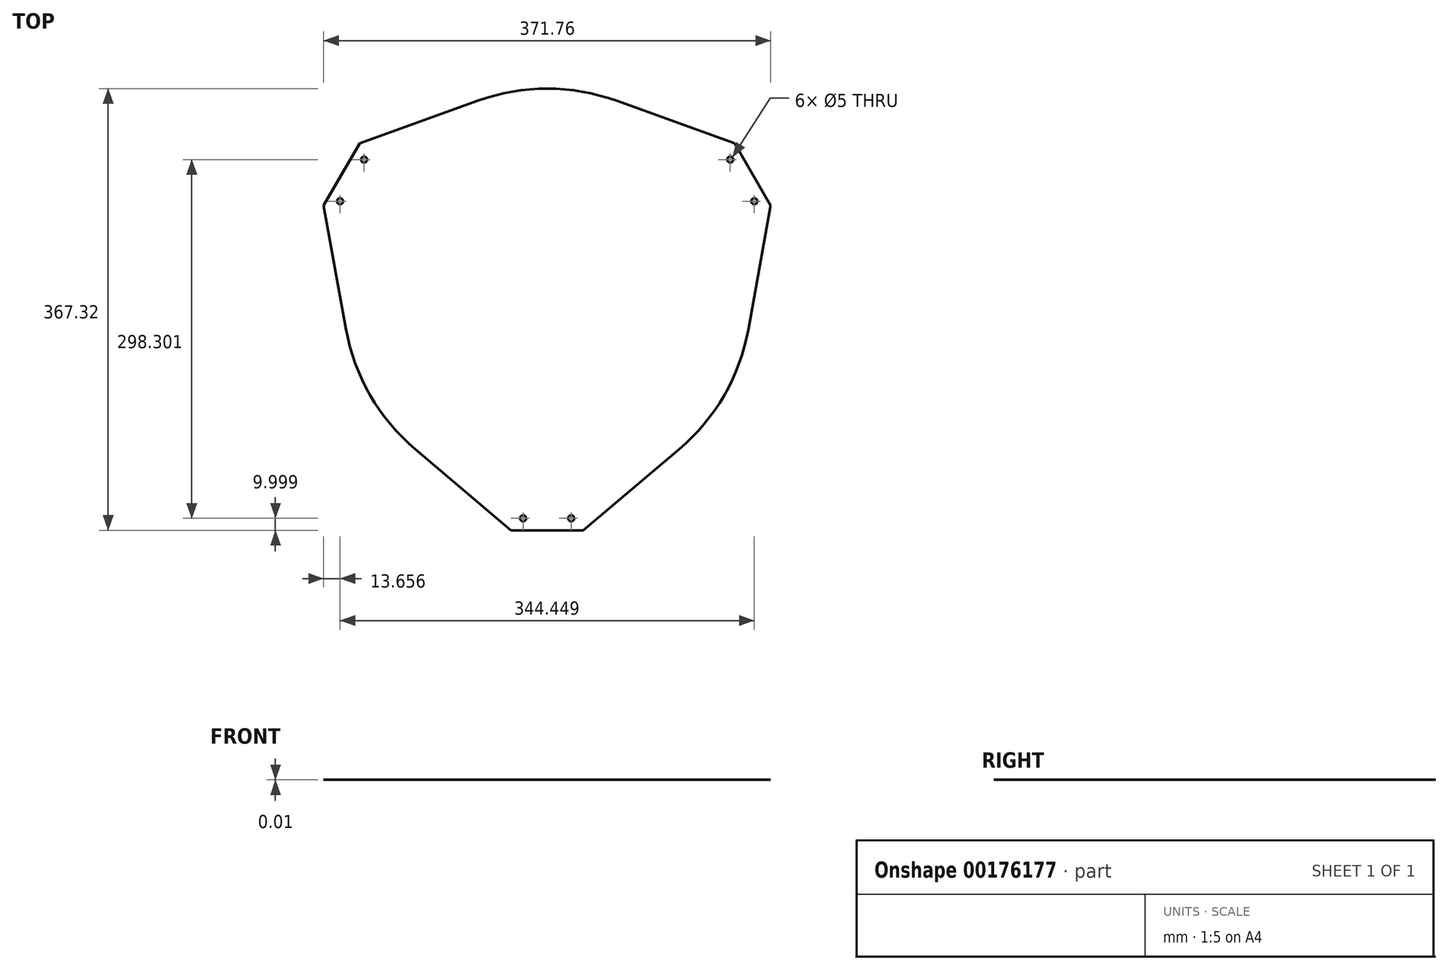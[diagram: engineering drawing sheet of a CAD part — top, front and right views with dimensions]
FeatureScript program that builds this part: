
annotation { "Feature Type Name" : "Feature", "Feature Type Description" : "" }
export const myFeature = defineFeature(function(context is Context, id is Id, definition is map)
    precondition{}
    {
        {
            var Q0;
            Q0=qCreatedBy(makeId("Top.planeOp"),FACE);
            var sketch = newSketch(context, id + "F0", { "sketchPlane" : qUnion([Q0])});
            skLineSegment(sketch, "E0.top", {"start": v(0, -197.32) * mm, "end": v(60, -197.32) * mm});
            skCircle(sketch, "E1", {"center": v(10, -187.32) * mm, "radius": 2.5 * mm});
            skCircle(sketch, "E2", {"center": v(50, -187.32) * mm, "radius": 2.5 * mm});
            skLineSegment(sketch, "E3", {"start": v(-155.88, 72.68) * mm, "end": v(-125.88, 124.64) * mm});
            skLineSegment(sketch, "E4", {"start": v(185.88, 124.64) * mm, "end": v(215.88, 72.68) * mm});
            skCircle(sketch, "E5", {"center": v(-122.22, 110.98) * mm, "radius": 2.5 * mm});
            skCircle(sketch, "E6", {"center": v(-142.22, 76.34) * mm, "radius": 2.5 * mm});
            skCircle(sketch, "E7", {"center": v(182.22, 110.98) * mm, "radius": 2.5 * mm});
            skCircle(sketch, "E8", {"center": v(202.22, 76.34) * mm, "radius": 2.5 * mm});
            skArc(sketch, "E9", {"start": v(-137.3, -30.23) * mm, "mid": v(-117.22, -85) * mm, "end": v(-79.82, -129.77) * mm});
            skLineSegment(sketch, "E10", {"start": v(-125.88, 124.64) * mm, "end": v(-27.47, 160) * mm});
            skLineSegment(sketch, "E11", {"start": v(185.88, 124.64) * mm, "end": v(87.47, 160) * mm});
            skLineSegment(sketch, "E12", {"start": v(-155.88, 72.68) * mm, "end": v(-137.3, -30.23) * mm});
            skLineSegment(sketch, "E13", {"start": v(215.88, 72.68) * mm, "end": v(197.3, -30.23) * mm});
            skLineSegment(sketch, "E14", {"start": v(60, -197.32) * mm, "end": v(139.82, -129.77) * mm});
            skLineSegment(sketch, "E15", {"start": v(0, -197.32) * mm, "end": v(-79.82, -129.77) * mm});
            skArc(sketch, "E16.trimOffspring", {"start": v(139.82, -129.77) * mm, "mid": v(177.22, -85) * mm, "end": v(197.3, -30.23) * mm});
            skArc(sketch, "E17.trimOffspring", {"start": v(87.47, 160) * mm, "mid": v(30, 170) * mm, "end": v(-27.47, 160) * mm});
            skLineSegment(sketch, "E18", {"start": v(30, 0) * mm, "end": v(30, -197.32) * mm, "construction": true});
            skLineSegment(sketch, "E19", {"start": v(30, 0) * mm, "end": v(200.88, 98.66) * mm, "construction": true});
            skLineSegment(sketch, "E20", {"start": v(30, 0) * mm, "end": v(-140.88, 98.66) * mm, "construction": true});
            skSolve(sketch);
        }
        {
            var Q0;
            Q0=makeQuery(id+"F0.imprint","IMPRINT",FACE,{"disambiguationData":[TD([[makeQuery(id+"F0.imprint","IMPRINT",EDGE,{"derivedFrom":sQuery(id+"F0.wireOp",EDGE,"E0.top")}),1.0]])]});
            extrude(context, id + "F1", {"entities" : qUnion([Q0]), "depth" : 1 / 101.6 * mm});
        }
    });
